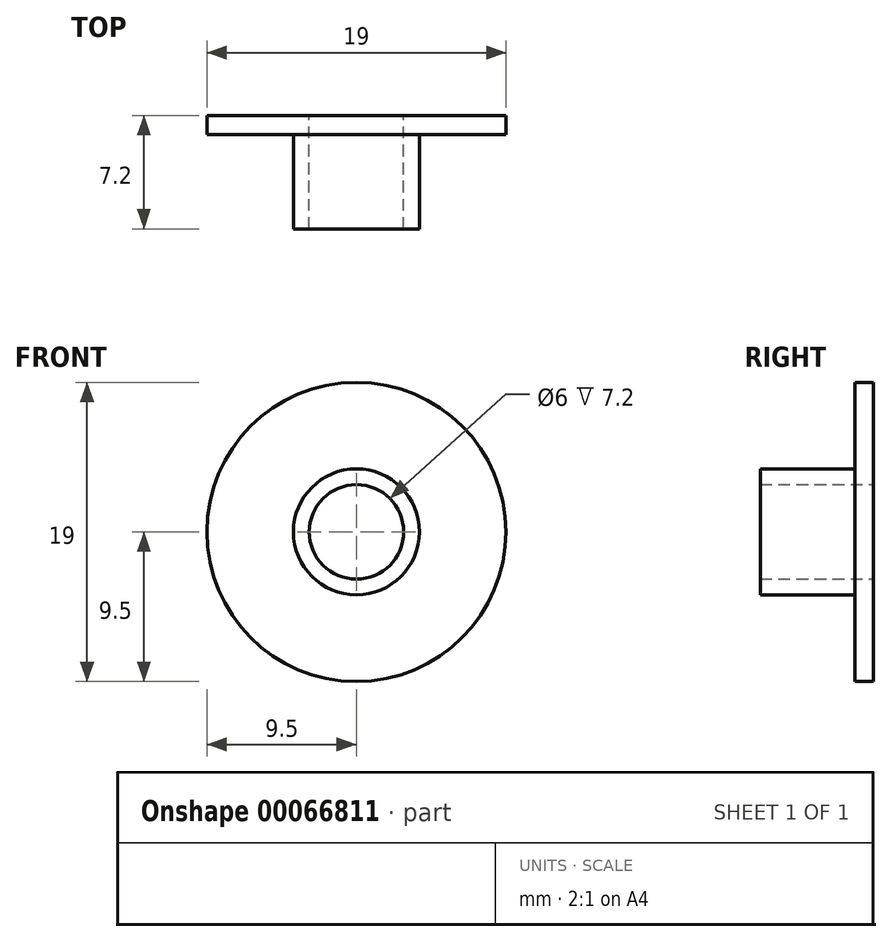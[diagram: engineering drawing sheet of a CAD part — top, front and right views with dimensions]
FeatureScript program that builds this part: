
annotation { "Feature Type Name" : "Feature", "Feature Type Description" : "" }
export const myFeature = defineFeature(function(context is Context, id is Id, definition is map)
    precondition{}
    {
        {
            var Q0;
            Q0=qCreatedBy(makeId("Front.planeOp"),FACE);
            var sketch = newSketch(context, id + "F0", { "sketchPlane" : qUnion([Q0])});
            skCircle(sketch, "E0", {"center": v(0, 0) * mm, "radius": 9.5 * mm});
            skCircle(sketch, "E1", {"center": v(0, 0) * mm, "radius": 3 * mm});
            skCircle(sketch, "E2", {"center": v(0, 0) * mm, "radius": 4 * mm});
            skSolve(sketch);
        }
        {
            var Q0;
            Q0=makeQuery(id+"F0.imprint","IMPRINT",FACE,{"disambiguationData":[TD([[makeQuery(id+"F0.imprint","IMPRINT",EDGE,{"derivedFrom":sQuery(id+"F0.wireOp",EDGE,"E0")}),1.0]])]});
            extrude(context, id + "F1", {"entities" : qUnion([Q0]), "oppositeDirection" : true, "depth" : 1.2 * mm});
        }
        {
            var Q0;
            Q0=makeQuery(id+"F0.imprint","IMPRINT",FACE,{"disambiguationData":[TD([[makeQuery(id+"F0.imprint","IMPRINT",EDGE,{"derivedFrom":sQuery(id+"F0.wireOp",EDGE,"E1")}),-1.0]])]});
            extrude(context, id + "F2", {"entities" : qUnion([Q0]), "operationType" : NewBodyOperationType.ADD, "depth" : 6 * mm, "hasSecondDirection" : true, "secondDirectionOppositeDirection" : true, "secondDirectionDepth" : 1.2 * mm});
        }
    });
